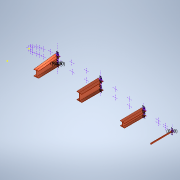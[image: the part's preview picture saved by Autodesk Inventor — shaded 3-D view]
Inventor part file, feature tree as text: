
AUTODESK INVENTOR PART (.ipt)
format: ipt  version: 2022 (Build 260153000, 153)  size: 408,576 bytes
history: native  units: mm
features: sketch x17, thicken_offset x12, loft x5, plane x1
ambient origin geometry x8: Origin, YZ Plane, XZ Plane, XY Plane, X Axis, Y Axis, Z Axis, Center Point
bodies: Body1 (feature_tree)
feature tree (35):
  sketch  "Sketch3"  dims[d29=150.0mm d35=2.0mm]
  sketch  "Sketch4"  dims[d36=90.0deg d37=2.0mm]
  sketch  "Sketch5"  dims[d38=90.0deg d43=2.0mm]
  sketch  "Sketch6"  dims[d44=2.0mm d51=2.0mm]
  plane  "Work Plane2"
  sketch  "Sketch9"  dims[d52=2.0mm d56=2.0mm]
  sketch  "Sketch10"  dims[d57=2.0mm]
  sketch  "Sketch14"  dims[d65=2.0mm]
  sketch  "Sketch15"  dims[d66=2.0mm]
  sketch  "Sketch16"  dims[d69=2.0mm]
  sketch  "Sketch17"  dims[d70=2.0mm]
  sketch  "Sketch18"  dims[d76=2.0mm]
  sketch  "Sketch19"  dims[d77=0.0mm]
  sketch  "Sketch20"  dims[d150=1.8mm]
  sketch  "Sketch21"  dims[d151=1.8mm]
  loft  "Loft2"
  loft  "Loft3"
  loft  "Loft4"
  loft  "Loft5"
  thicken_offset  "Thicken2"
  thicken_offset  "Thicken3"
  thicken_offset  "Thicken4"
  thicken_offset  "Thicken5"
  thicken_offset  "Thicken6"
  thicken_offset  "Thicken7"
  thicken_offset  "Thicken8"
  thicken_offset  "Thicken9"
  thicken_offset  "Thicken10"
  thicken_offset  "Thicken12"
  thicken_offset  "Thicken13"
  thicken_offset  "Thicken14"
  sketch  "Sketch22"  dims[d156=1.8mm]
  sketch  "Sketch23"  dims[d157=1.8mm]
  loft  "Loft6"
  sketch  "Sketch24"  dims[d167=1.8mm d168=90.0deg d169=1.8mm d170=90.0deg d175=1.8mm d176=1.8mm d187=1.8mm d188=1.8mm d193=1.8mm d194=90.0deg d195=1.8mm d196=90.0deg d201=0.0mm d202=90.0deg d203=0.0mm d204=90.0deg d205=0.0mm d206=90.0deg d207=0.0mm d208=90.0deg d209=0.0mm d210=90.0deg d211=0.0mm d212=90.0deg d213=0.0mm d214=90.0deg d215=0.0mm d216=90.0deg d217=12.5mm d218=12.5mm d219=12.5mm d220=12.5mm d221=12.5mm d222=12.5mm d223=12.5mm d224=12.5mm d225=12.5mm d226=12.5mm d227=12.5mm d228=12.5mm d229=12.5mm d230=12.5mm d231=12.5mm d232=12.5mm d233=10.0mm d234=10.0mm d237=10.0mm d238=10.0mm d239=10.0mm d240=10.0mm d241=10.0mm d242=10.0mm d243=0.0mm d244=90.0deg d245=0.0mm d246=90.0deg d6=0.5mm d7=0.872665mm d8=0.5mm d9=0.872665mm]
